# Revit family: LC-9
name_source: partatom
category: Generic Models
revit_build: Autodesk Revit 2017 (Build: 20170419_0315(x64)
units: mm (PartAtom-declared; Revit-internal decimal feet)

## family parameters
Always vertical = Yes
Can host rebar = No
Cut with Voids When Loaded = No
Host = Wall
Part Type = Normal
Room Calculation Point = No
Round Connector Dimension = Use Diameter
Shared = No

## types (3) — shared parameters
Depth = 88 mm  [stored 0.288714 ft]
Height = 1200 mm  [stored 3.93701 ft]
Keynote = 6120
Manufacturer = Sentakia Oy
Materiaali = kromattu messinki (CuZn36As)
Sentakia_Material_Default = Stainless Steel, Polished_sentakia

## per-type parameters (varying)
| type | 350 | 500 | 600 | EAN | LVI | Leveys | Model | Teho | URL |
| 350 | Yes | No | No | 4770046007580 | 5489948 | 350 mm | LS-9/350 | kromi: 150 W maalattu: 195 W | http://www.sentakia.com |
| 500 | No | Yes | No | 4770046007597 | 5489949 | 500 mm  [stored 1.64042 ft] | LS-9/500 | kromi: 167 W maalattu: 217 W | www.sentakia.com |
| 600 | No | No | Yes | 4770046007177 | 5489950 | 600 mm | LS-9/600 | kromi: 180 W maalattu: 234 W | www.sentakia.com |

note: [stored X ft] marks values corroborated as IEEE doubles in the binary element streams (Revit-internal decimal feet)

## geometry (parser evidence)
native form markers: Blend x4, Sweep x3
no freeform markers — native parametric forms only
